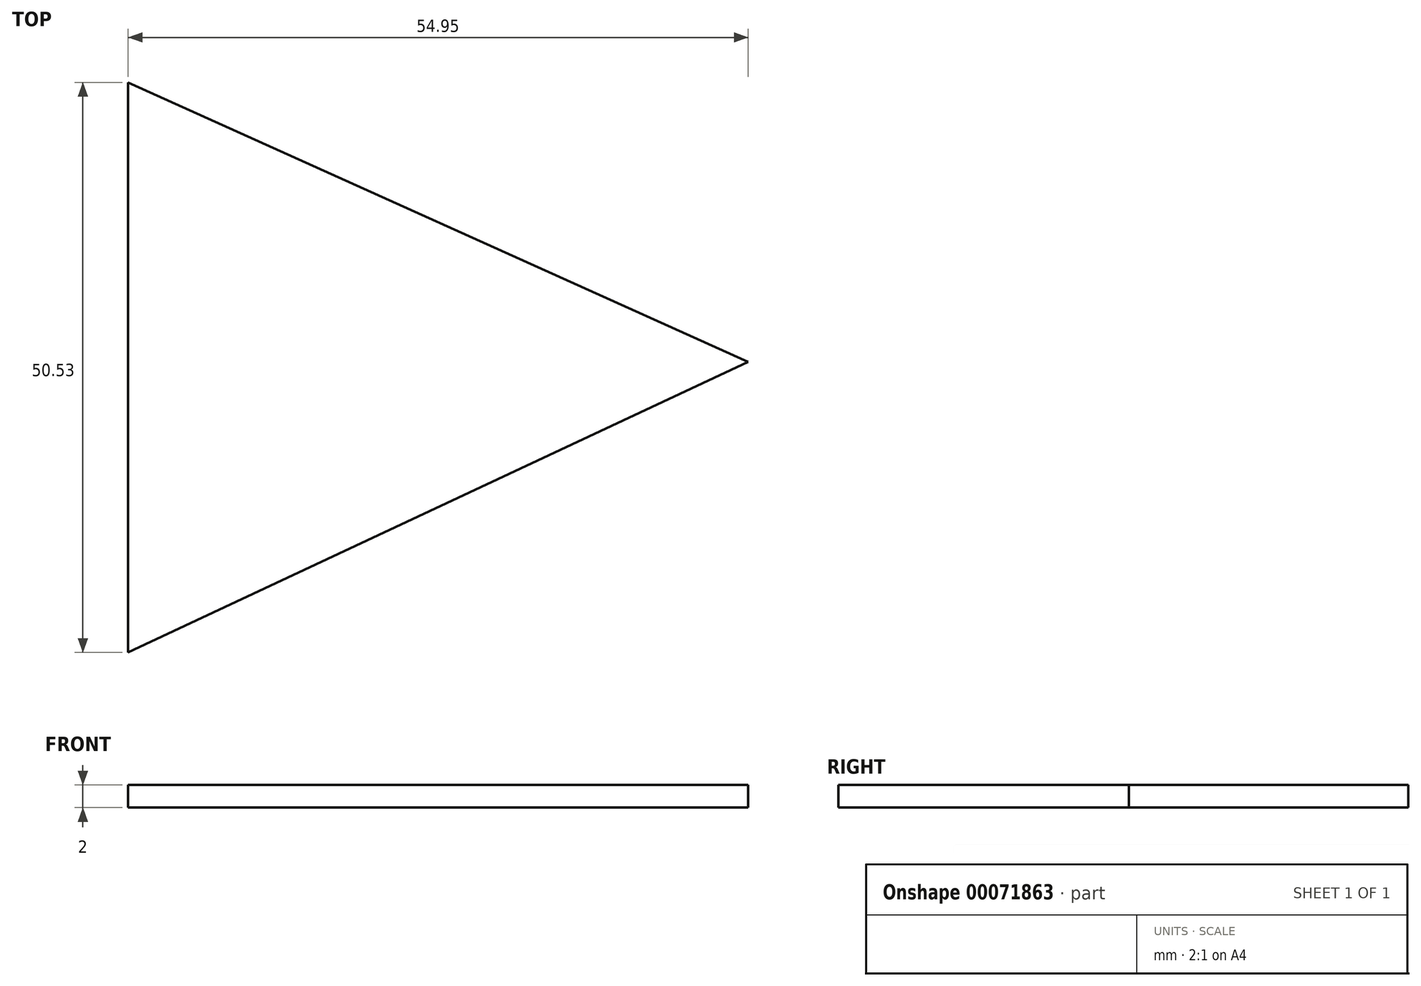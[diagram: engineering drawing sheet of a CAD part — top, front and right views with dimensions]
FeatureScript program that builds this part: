
annotation { "Feature Type Name" : "Feature", "Feature Type Description" : "" }
export const myFeature = defineFeature(function(context is Context, id is Id, definition is map)
    precondition{}
    {
        {
            var Q0;
            Q0=qCreatedBy(makeId("Top.planeOp"),FACE);
            var sketch = newSketch(context, id + "F0", { "sketchPlane" : qUnion([Q0])});
            skLineSegment(sketch, "E0", {"start": v(0, 24.78) * mm, "end": v(0, -25.75) * mm});
            skLineSegment(sketch, "E1", {"start": v(0, -25.75) * mm, "end": v(54.95, 0) * mm});
            skLineSegment(sketch, "E2", {"start": v(54.95, 0) * mm, "end": v(0, 24.78) * mm});
            skSolve(sketch);
        }
        {
            var Q0;
            Q0=makeQuery(id+"F0.imprint","IMPRINT",FACE,{"disambiguationData":[TD([[makeQuery(id+"F0.imprint","IMPRINT",EDGE,{"derivedFrom":sQuery(id+"F0.wireOp",EDGE,"E0")}),1.0]])]});
            extrude(context, id + "F1", {"entities" : qUnion([Q0]), "depth" : 2 * mm});
        }
    });
